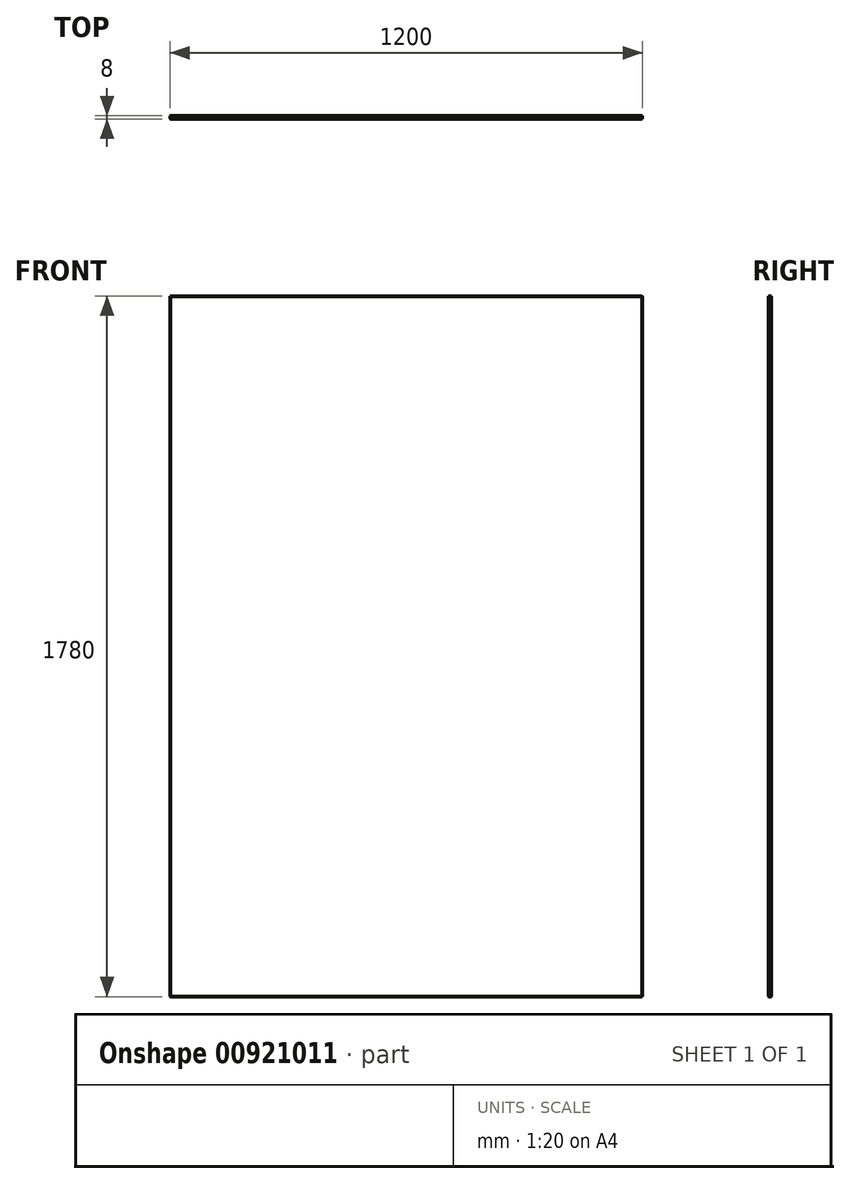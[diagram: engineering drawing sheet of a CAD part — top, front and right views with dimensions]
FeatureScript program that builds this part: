
annotation { "Feature Type Name" : "Feature", "Feature Type Description" : "" }
export const myFeature = defineFeature(function(context is Context, id is Id, definition is map)
    precondition{}
    {
        {
            var Q0;
            Q0=qCreatedBy(makeId("Top.planeOp"),FACE);
            var sketch = newSketch(context, id + "F0", { "sketchPlane" : qUnion([Q0])});
            skLineSegment(sketch, "E0.bottom", {"start": v(-890, 600) * mm, "end": v(890, 600) * mm});
            skLineSegment(sketch, "E0.top", {"start": v(-890, -600) * mm, "end": v(890, -600) * mm});
            skLineSegment(sketch, "E0.left", {"start": v(-890, 600) * mm, "end": v(-890, -600) * mm});
            skLineSegment(sketch, "E0.right", {"start": v(890, 600) * mm, "end": v(890, -600) * mm});
            skPoint(sketch, "E0.middle", {"position": v(0, 0) * mm});
            skSolve(sketch);
        }
        {
            var Q0;
            Q0=makeQuery(id+"F0.imprint","IMPRINT",FACE,{"disambiguationData":[TD([[makeQuery(id+"F0.imprint","IMPRINT",EDGE,{"derivedFrom":sQuery(id+"F0.wireOp",EDGE,"E0.bottom")}),-1.0]])]});
            extrude(context, id + "F1", {"entities" : qUnion([Q0]), "endBound" : BoundingType.SYMMETRIC, "depth" : 8 * mm, "offsetDistance" : 25 * mm});
        }
        {
            var Q0;
            Q0=makeQuery(id+"F1.opExtrude","CAP_EDGE",EDGE,{"disambiguationData":[OSD([sQuery(id+"F0.wireOp",EDGE,"E0.right")])],"isStart":true});
            var Q1;
            Q1=makeQuery(id+"F1.opExtrude","CAP_EDGE",EDGE,{"disambiguationData":[OSD([sQuery(id+"F0.wireOp",EDGE,"E0.top")])],"isStart":true});
            var Q2;
            Q2=makeQuery(id+"F1.opExtrude","CAP_EDGE",EDGE,{"disambiguationData":[OSD([sQuery(id+"F0.wireOp",EDGE,"E0.left")])],"isStart":true});
            var Q3;
            Q3=makeQuery(id+"F1.opExtrude","CAP_EDGE",EDGE,{"disambiguationData":[OSD([sQuery(id+"F0.wireOp",EDGE,"E0.bottom")])],"isStart":true});
            chamfer(context, id + "F2", {"entities" : qUnion([Q0, Q1, Q2, Q3]), "width" : 1 * mm, "tangentPropagation" : true});
        }
        {
            var Q0;
            Q0=makeQuery(id+"F1.opExtrude","SWEPT_EDGE",EDGE,{"disambiguationData":[OSD([sQuery(id+"F0.wireOp",EDGE,"E0.top"),sQuery(id+"F0.wireOp",EDGE,"E0.right")])]});
            chamfer(context, id + "F3", {"entities" : qUnion([Q0]), "width" : 1 * mm, "tangentPropagation" : true});
        }
        {
            var Q0;
            Q0=makeQuery(id+"F1.opExtrude","SWEPT_EDGE",EDGE,{"disambiguationData":[OSD([sQuery(id+"F0.wireOp",EDGE,"E0.bottom"),sQuery(id+"F0.wireOp",EDGE,"E0.left")])]});
            chamfer(context, id + "F4", {"entities" : qUnion([Q0]), "width" : 1 * mm, "tangentPropagation" : true});
        }
        {
            var Q0;
            Q0=makeQuery(id+"F1.opExtrude","SWEPT_EDGE",EDGE,{"disambiguationData":[OSD([sQuery(id+"F0.wireOp",EDGE,"E0.top"),sQuery(id+"F0.wireOp",EDGE,"E0.left")])]});
            chamfer(context, id + "F5", {"entities" : qUnion([Q0]), "width" : 1 * mm, "tangentPropagation" : true});
        }
        {
            var Q0;
            Q0=makeQuery(id+"F1.opExtrude","SWEPT_EDGE",EDGE,{"disambiguationData":[OSD([sQuery(id+"F0.wireOp",EDGE,"E0.bottom"),sQuery(id+"F0.wireOp",EDGE,"E0.right")])]});
            chamfer(context, id + "F6", {"entities" : qUnion([Q0]), "width" : 1 * mm, "tangentPropagation" : true});
        }
        {
            var Q0;
            Q0=makeQuery(id+"F1.opExtrude","CAP_EDGE",EDGE,{"disambiguationData":[OSD([sQuery(id+"F0.wireOp",EDGE,"E0.top")])],"isStart":false});
            var Q1;
            Q1=makeQuery(id+"F1.opExtrude","CAP_EDGE",EDGE,{"disambiguationData":[OSD([sQuery(id+"F0.wireOp",EDGE,"E0.right")])],"isStart":false});
            var Q2;
            Q2=makeQuery(id+"F1.opExtrude","CAP_EDGE",EDGE,{"disambiguationData":[OSD([sQuery(id+"F0.wireOp",EDGE,"E0.bottom")])],"isStart":false});
            var Q3;
            Q3=makeQuery(id+"F1.opExtrude","CAP_EDGE",EDGE,{"disambiguationData":[OSD([sQuery(id+"F0.wireOp",EDGE,"E0.left")])],"isStart":false});
            chamfer(context, id + "F7", {"entities" : qUnion([Q0, Q1, Q2, Q3]), "width" : 1 * mm, "tangentPropagation" : true});
        }
        {
            var Q0;
            Q0=makeQuery(id+"F1.opExtrude","SWEPT_BODY",BODY,{"disambiguationData":[OSD([sQuery(id+"F0.wireOp",EDGE,"E0.bottom"),sQuery(id+"F0.wireOp",EDGE,"E0.top"),sQuery(id+"F0.wireOp",EDGE,"E0.left"),sQuery(id+"F0.wireOp",EDGE,"E0.right")])]});
            var Q1;
            {var subQ0=sQuery(id+"F0.wireOp",EDGE,"E0.right");Q1=makeQuery(id+"F7.opChamfer","BLEND_EDGE",EDGE,{"blendedFrom":[makeQuery(id+"F1.opExtrude","CAP_EDGE",EDGE,{"disambiguationData":[OSD([subQ0])],"isStart":false}),makeQuery(id+"F1.opExtrude","CAP_FACE",FACE,{"disambiguationData":[OSD([sQuery(id+"F0.wireOp",EDGE,"E0.bottom"),sQuery(id+"F0.wireOp",EDGE,"E0.top"),sQuery(id+"F0.wireOp",EDGE,"E0.left"),subQ0])],"isStart":false})],"blendedInto":[makeQuery(id+"F1.opExtrude","CAP_FACE",FACE,{"disambiguationData":[OSD([sQuery(id+"F0.wireOp",EDGE,"E0.bottom"),sQuery(id+"F0.wireOp",EDGE,"E0.top"),sQuery(id+"F0.wireOp",EDGE,"E0.left"),subQ0])],"isStart":false})]});}
            transform(context, id + "F8", {"entities" : qUnion([Q0]), "transformType" : TransformType.ROTATION, "transformAxis" : qUnion([Q1]), "angle" : 90 * degree, "makeCopy" : false});
        }
        {
            var Q0;
            Q0=makeQuery(id+"F1.opExtrude","SWEPT_BODY",BODY,{"disambiguationData":[OSD([sQuery(id+"F0.wireOp",EDGE,"E0.bottom"),sQuery(id+"F0.wireOp",EDGE,"E0.top"),sQuery(id+"F0.wireOp",EDGE,"E0.left"),sQuery(id+"F0.wireOp",EDGE,"E0.right")])]});
            var Q1;
            {var subQ0=sQuery(id+"F0.wireOp",EDGE,"E0.bottom");Q1=makeQuery(id+"F2.opChamfer","BLEND_EDGE",EDGE,{"blendedFrom":[makeQuery(id+"F1.opExtrude","CAP_EDGE",EDGE,{"disambiguationData":[OSD([subQ0])],"isStart":true}),makeQuery(id+"F1.opExtrude","SWEPT_FACE",FACE,{"disambiguationData":[OSD([subQ0])]})],"blendedInto":[makeQuery(id+"F1.opExtrude","SWEPT_FACE",FACE,{"disambiguationData":[OSD([subQ0])]})]});}
            transform(context, id + "F9", {"entities" : qUnion([Q0]), "transformType" : TransformType.ROTATION, "transformAxis" : qUnion([Q1]), "angle" : 270 * degree, "makeCopy" : false});
        }
    });
